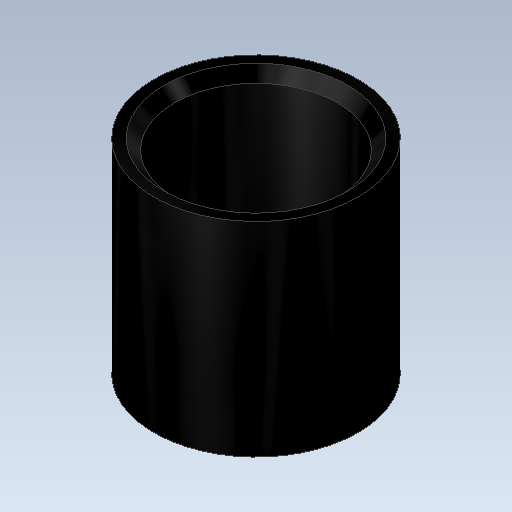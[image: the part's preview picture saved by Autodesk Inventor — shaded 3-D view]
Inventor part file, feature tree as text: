
AUTODESK INVENTOR PART (.ipt)
format: ipt  version: 2020.1 (Build 241239000, 239)  size: 136,704 bytes
history: native  units: mm
features: extrude x1, chamfer x1, sketch x1
ambient origin geometry x8: Origin, YZ Plane, XZ Plane, XY Plane, X Axis, Y Axis, Z Axis, Center Point
bodies: Solid1 (feature_tree)
feature tree (3):
  extrude  "Extrusion1"  Depth=10.0mm
  chamfer  "Chamfer1"  Distance=10.0mm
  sketch  "Sketch1"  dims[d0=8.0mm d1=10.0mm d2=10.0mm d3=0.0mm d4=0.5mm d5=2.0mm d6=45.0deg]
